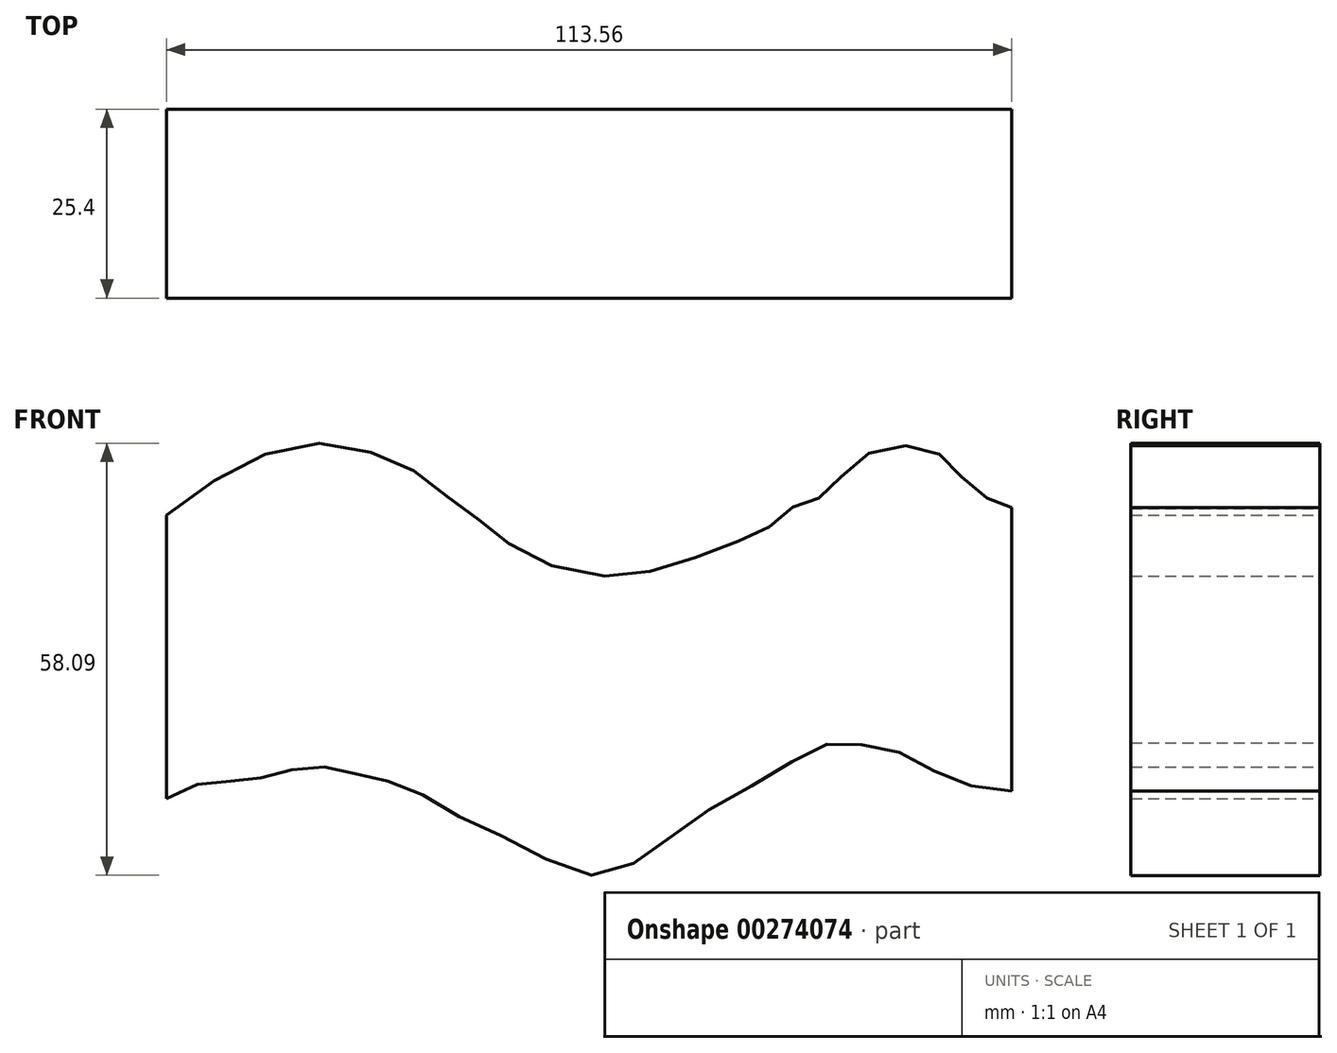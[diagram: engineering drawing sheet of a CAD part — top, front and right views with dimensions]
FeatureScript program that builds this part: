
annotation { "Feature Type Name" : "Feature", "Feature Type Description" : "" }
export const myFeature = defineFeature(function(context is Context, id is Id, definition is map)
    precondition{}
    {
        {
            var Q0;
            Q0=qCreatedBy(makeId("Front.planeOp"),FACE);
            var sketch = newSketch(context, id + "F0", { "sketchPlane" : qUnion([Q0])});
            skLineSegment(sketch, "E0", {"start": v(-57.15, 0) * mm, "end": v(-57.15, 38.1) * mm});
            skLineSegment(sketch, "E1", {"start": v(56.41, 0.98) * mm, "end": v(56.41, 39.08) * mm});
            skFitSpline(sketch, "E2", {"points": [v(56.41, 39.08) * mm, v(54.38, 39.64) * mm, v(51.43, 41.66) * mm, v(48.85, 44.06) * mm, v(46.46, 46.46) * mm, v(42.4, 47.38) * mm, v(37.6, 46.64) * mm, v(33.92, 43.5) * mm, v(31.7, 42.03) * mm, v(29.13, 39.08) * mm, v(26.55, 39.08) * mm, v(23.97, 36.69) * mm, v(20.83, 35.03) * mm, v(14.56, 32.63) * mm, v(7.37, 30.42) * mm, v(0, 30.05) * mm, v(-9.4, 33) * mm, v(-13.64, 36.32) * mm, v(-17.88, 39.27) * mm, v(-22.3, 42.95) * mm, v(-28.4, 46.09) * mm, v(-37.42, 47.75) * mm, v(-47.56, 44.61) * mm, v(-57.15, 38.1) * mm], "startDerivative": vector(-63.35, 50.25) * mm, "endDerivative": vector(-145.77, -110.94) * mm});
            skFitSpline(sketch, "E3", {"points": [v(-57.15, 0) * mm, v(-52.54, 2.03) * mm, v(-47.56, 2.4) * mm, v(-43.7, 2.95) * mm, v(-39.27, 4.06) * mm, v(-34.66, 4.06) * mm, v(-30.42, 2.95) * mm, v(-25.07, 1.66) * mm, v(-18.62, -2.03) * mm, v(-9.96, -6.08) * mm, v(0, -10.32) * mm, v(7.93, -7.19) * mm, v(15.49, -1.66) * mm, v(24.7, 3.5) * mm, v(31.16, 7.19) * mm, v(36.69, 7.19) * mm, v(42.95, 5.53) * mm, v(49.22, 2.03) * mm, v(56.41, 0.98) * mm], "startDerivative": vector(98.39, 60.36) * mm, "endDerivative": vector(116.63, -38.25) * mm});
            skSolve(sketch);
        }
        {
            var Q0;
            Q0=makeQuery(id+"F0.imprint","IMPRINT",FACE,{"disambiguationData":[TD([[makeQuery(id+"F0.imprint","IMPRINT",EDGE,{"derivedFrom":sQuery(id+"F0.wireOp",EDGE,"E0")}),-1.0]])]});
            extrude(context, id + "F1", {"entities" : qUnion([Q0]), "depth" : 25.4 * mm});
        }
    });
